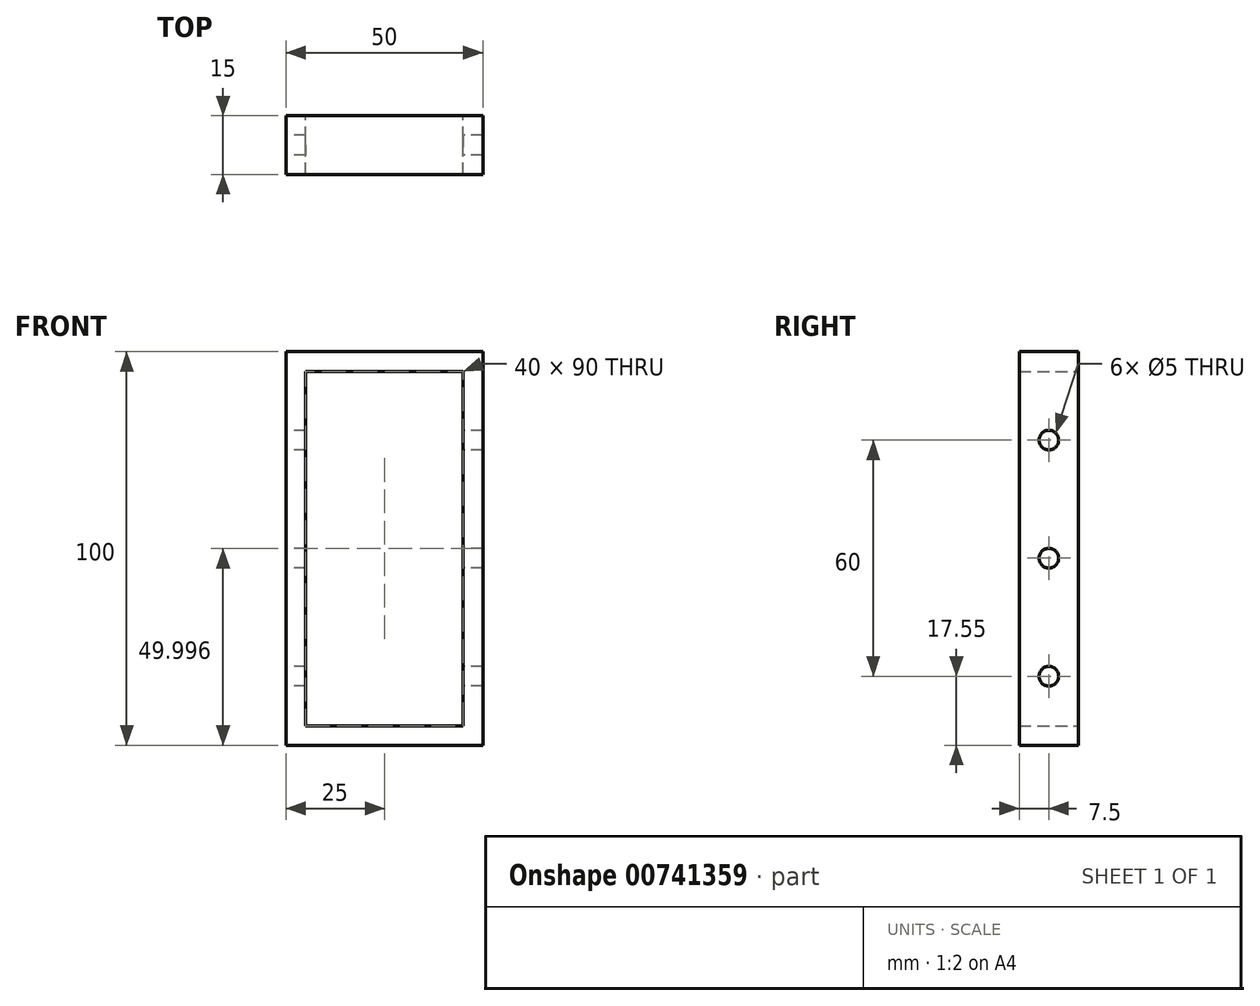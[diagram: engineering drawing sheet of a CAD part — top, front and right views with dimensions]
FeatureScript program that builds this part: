
annotation { "Feature Type Name" : "Feature", "Feature Type Description" : "" }
export const myFeature = defineFeature(function(context is Context, id is Id, definition is map)
    precondition{}
    {
        {
            var Q0;
            Q0=qCreatedBy(makeId("Front.planeOp"),FACE);
            var sketch = newSketch(context, id + "F0", { "sketchPlane" : qUnion([Q0])});
            skLineSegment(sketch, "E0.bottom", {"start": v(-25.14, 52.45) * mm, "end": v(24.86, 52.45) * mm});
            skLineSegment(sketch, "E0.top", {"start": v(-25.14, -47.55) * mm, "end": v(24.86, -47.55) * mm});
            skLineSegment(sketch, "E0.left", {"start": v(-25.14, 52.45) * mm, "end": v(-25.14, -47.55) * mm});
            skLineSegment(sketch, "E0.right", {"start": v(24.86, 52.45) * mm, "end": v(24.86, -47.55) * mm});
            skLineSegment(sketch, "E1.0", {"start": v(-20.14, 47.45) * mm, "end": v(19.86, 47.45) * mm});
            skLineSegment(sketch, "E1.1", {"start": v(-20.14, 47.45) * mm, "end": v(-20.14, -42.55) * mm});
            skLineSegment(sketch, "E1.2", {"start": v(-20.14, -42.55) * mm, "end": v(19.86, -42.55) * mm});
            skLineSegment(sketch, "E1.3", {"start": v(19.86, 47.45) * mm, "end": v(19.86, -42.55) * mm});
            skSolve(sketch);
        }
        {
            var Q0;
            Q0=makeQuery(id+"F0.imprint","IMPRINT",FACE,{"disambiguationData":[TD([[makeQuery(id+"F0.imprint","IMPRINT",EDGE,{"derivedFrom":sQuery(id+"F0.wireOp",EDGE,"E0.bottom")}),-1.0]])]});
            extrude(context, id + "F1", {"entities" : qUnion([Q0]), "depth" : 15 * mm, "offsetDistance" : 25 * mm});
        }
        {
            var Q0;
            Q0=makeQuery(id+"F1.opExtrude","SWEPT_FACE",FACE,{"disambiguationData":[OSD([sQuery(id+"F0.wireOp",EDGE,"E0.left")])]});
            var sketch = newSketch(context, id + "F2", { "sketchPlane" : qUnion([Q0])});
            skCircle(sketch, "E2", {"center": v(7.5, 0) * mm, "radius": 2.5 * mm});
            skCircle(sketch, "E3", {"center": v(7.5, 30) * mm, "radius": 2.5 * mm});
            skCircle(sketch, "E4", {"center": v(7.5, -30) * mm, "radius": 2.5 * mm});
            skSolve(sketch);
        }
        {
            var Q0;
            Q0=makeQuery(id+"F2.imprint","IMPRINT",FACE,{"disambiguationData":[TD([[makeQuery(id+"F2.imprint","IMPRINT",EDGE,{"derivedFrom":sQuery(id+"F2.wireOp",EDGE,"E3")}),1.0]])]});
            var Q1;
            Q1=makeQuery(id+"F2.imprint","IMPRINT",FACE,{"disambiguationData":[TD([[makeQuery(id+"F2.imprint","IMPRINT",EDGE,{"derivedFrom":sQuery(id+"F2.wireOp",EDGE,"E2")}),1.0]])]});
            var Q2;
            Q2=makeQuery(id+"F2.imprint","IMPRINT",FACE,{"disambiguationData":[TD([[makeQuery(id+"F2.imprint","IMPRINT",EDGE,{"derivedFrom":sQuery(id+"F2.wireOp",EDGE,"E4")}),1.0]])]});
            extrude(context, id + "F3", {"entities" : qUnion([Q0, Q1, Q2]), "operationType" : NewBodyOperationType.REMOVE, "endBound" : BoundingType.THROUGH_ALL, "oppositeDirection" : true, "depth" : 25 * mm, "offsetDistance" : 25 * mm});
        }
    });
